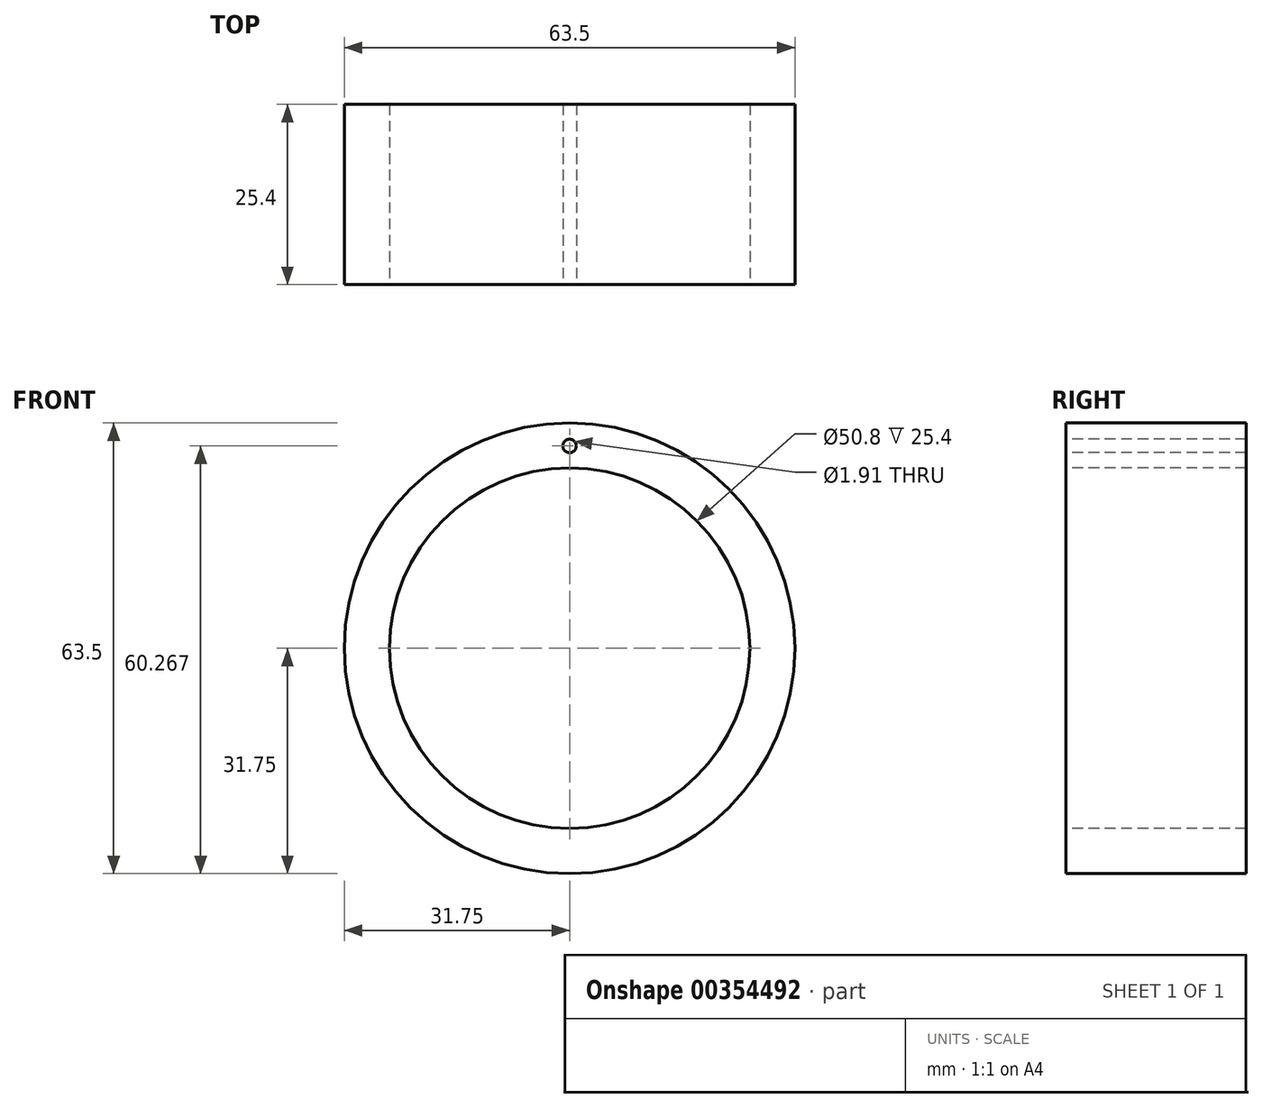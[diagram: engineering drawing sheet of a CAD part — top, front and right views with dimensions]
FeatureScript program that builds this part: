
annotation { "Feature Type Name" : "Feature", "Feature Type Description" : "" }
export const myFeature = defineFeature(function(context is Context, id is Id, definition is map)
    precondition{}
    {
        {
            var Q0;
            Q0=qCreatedBy(makeId("Front.planeOp"),FACE);
            var sketch = newSketch(context, id + "F0", { "sketchPlane" : qUnion([Q0])});
            skCircle(sketch, "E0", {"center": v(0, 0) * mm, "radius": 31.75 * mm});
            skCircle(sketch, "E1", {"center": v(0, 0) * mm, "radius": 25.4 * mm});
            skCircle(sketch, "E2", {"center": v(0, 0) * mm, "radius": 25.34 * mm});
            skCircle(sketch, "E3", {"center": v(0, 0) * mm, "radius": 19.05 * mm});
            skCircle(sketch, "E4", {"center": v(0, 0) * mm, "radius": 18.99 * mm});
            skCircle(sketch, "E5", {"center": v(0, 0) * mm, "radius": 12.7 * mm});
            skCircle(sketch, "E6", {"center": v(0, 28.52) * mm, "radius": 0.95 * mm});
            skCircle(sketch, "E7", {"center": v(0, 22.06) * mm, "radius": 0.95 * mm});
            skCircle(sketch, "E8", {"center": v(0, 15.61) * mm, "radius": 0.95 * mm});
            skSolve(sketch);
        }
        {
            var Q0;
            Q0=makeQuery(id+"F0.imprint","IMPRINT",FACE,{"disambiguationData":[TD([[makeQuery(id+"F0.imprint","IMPRINT",EDGE,{"derivedFrom":sQuery(id+"F0.wireOp",EDGE,"E0")}),1.0]])]});
            extrude(context, id + "F1", {"entities" : qUnion([Q0]), "oppositeDirection" : true, "depth" : 25.4 * mm});
        }
    });
